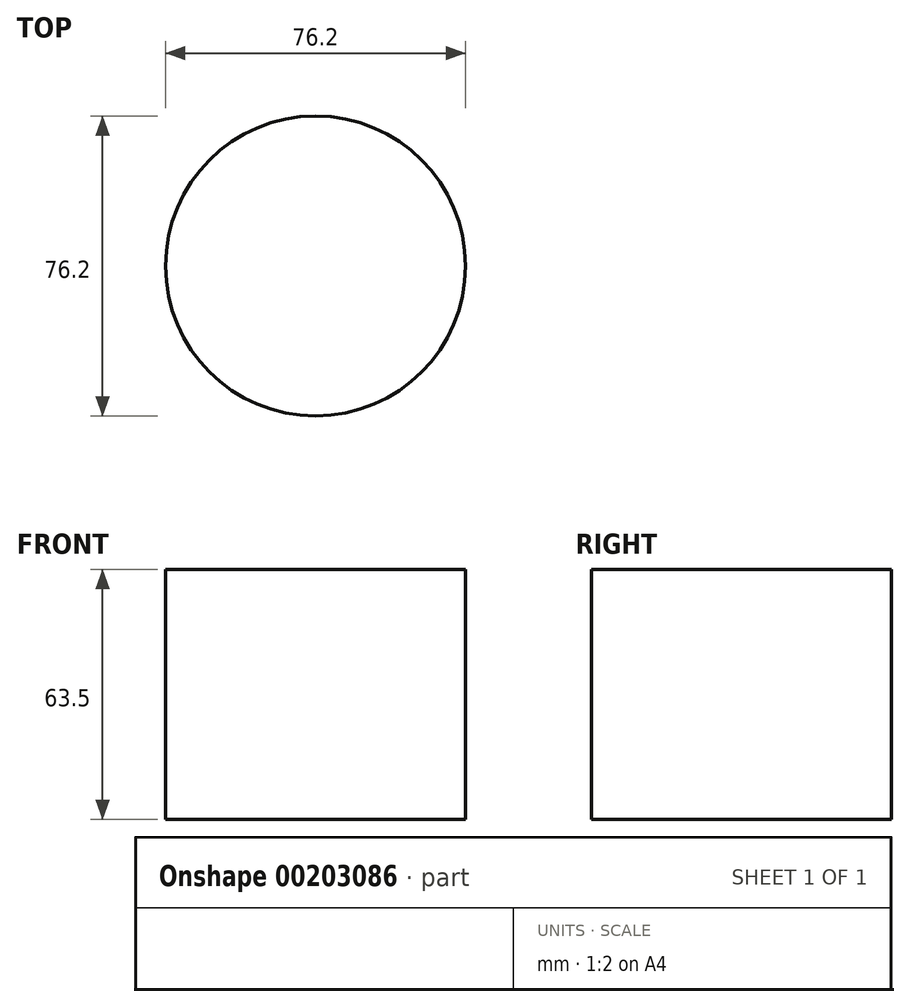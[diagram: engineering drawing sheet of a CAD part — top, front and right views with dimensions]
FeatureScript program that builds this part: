
annotation { "Feature Type Name" : "Feature", "Feature Type Description" : "" }
export const myFeature = defineFeature(function(context is Context, id is Id, definition is map)
    precondition{}
    {
        {
            var Q0;
            Q0=qCreatedBy(makeId("Top.planeOp"),FACE);
            var sketch = newSketch(context, id + "F0", { "sketchPlane" : qUnion([Q0])});
            skCircle(sketch, "E0", {"center": v(0, 0) * mm, "radius": 38.1 * mm});
            skSolve(sketch);
        }
        {
            var Q0;
            Q0=makeQuery(id+"F0.imprint","IMPRINT",FACE,{"disambiguationData":[TD([[makeQuery(id+"F0.imprint","IMPRINT",EDGE,{"derivedFrom":sQuery(id+"F0.wireOp",EDGE,"E0")}),1.0]])]});
            extrude(context, id + "F1", {"entities" : qUnion([Q0]), "depth" : 63.5 * mm});
        }
    });
